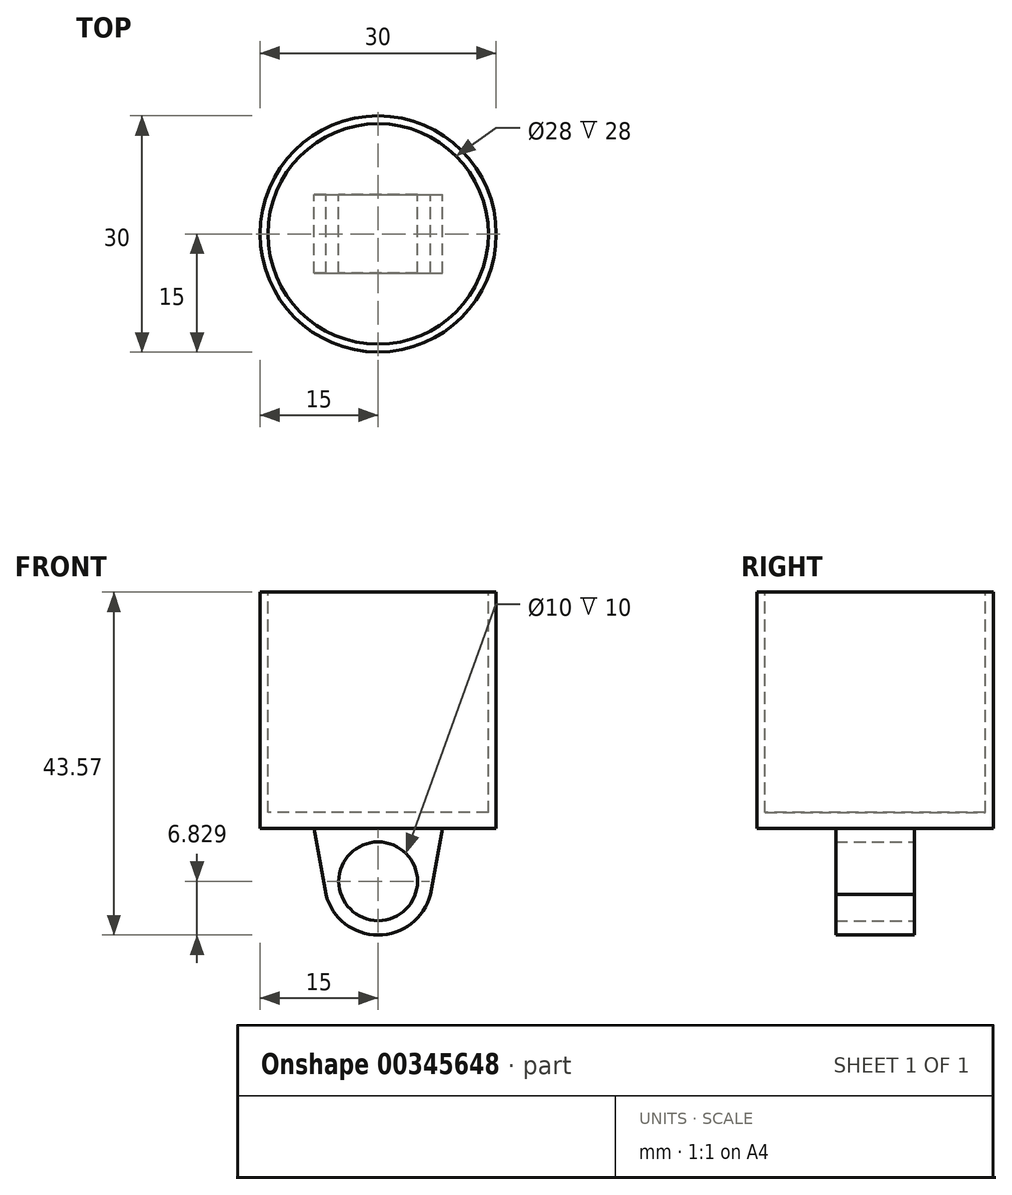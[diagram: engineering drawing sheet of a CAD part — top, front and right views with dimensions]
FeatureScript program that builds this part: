
annotation { "Feature Type Name" : "Feature", "Feature Type Description" : "" }
export const myFeature = defineFeature(function(context is Context, id is Id, definition is map)
    precondition{}
    {
        {
            var Q0;
            Q0=qCreatedBy(makeId("Top.planeOp"),FACE);
            var sketch = newSketch(context, id + "F0", { "sketchPlane" : qUnion([Q0])});
            skCircle(sketch, "E0", {"center": v(0, 0) * mm, "radius": 15 * mm});
            skSolve(sketch);
        }
        {
            var Q0;
            Q0=qSketchRegion(id+"F0",true);
            extrude(context, id + "F1", {"entities" : qUnion([Q0]), "depth" : 30 * mm});
        }
        {
            var Q0;
            Q0=makeQuery(id+"F1.opExtrude","CAP_FACE",FACE,{"disambiguationData":[OSD([sQuery(id+"F0.wireOp",EDGE,"E0")])],"isStart":false});
            var sketch = newSketch(context, id + "F2", { "sketchPlane" : qUnion([Q0])});
            skCircle(sketch, "E1", {"center": v(0, 0) * mm, "radius": 14 * mm});
            skSolve(sketch);
        }
        {
            var Q0;
            Q0=qSketchRegion(id+"F2",true);
            extrude(context, id + "F3", {"entities" : qUnion([Q0]), "operationType" : NewBodyOperationType.REMOVE, "oppositeDirection" : true, "depth" : 28 * mm});
        }
        {
            var Q0;
            Q0=qCreatedBy(makeId("Front.planeOp"),FACE);
            var sketch = newSketch(context, id + "F4", { "sketchPlane" : qUnion([Q0])});
            skArc(sketch, "E2", {"start": v(-6.62, -8.4) * mm, "mid": v(0, -13.57) * mm, "end": v(6.62, -8.4) * mm});
            skLineSegment(sketch, "E3", {"start": v(-6.62, -8.4) * mm, "end": v(-8.16, 0) * mm});
            skLineSegment(sketch, "E4", {"start": v(6.62, -8.4) * mm, "end": v(8.16, 0) * mm});
            skCircle(sketch, "E5", {"center": v(0, -6.74) * mm, "radius": 5 * mm});
            skLineSegment(sketch, "E6", {"start": v(-8.16, 0) * mm, "end": v(8.16, 0) * mm});
            skSolve(sketch);
        }
        {
            var Q0;
            Q0=qSketchRegion(id+"F4",true);
            extrude(context, id + "F5", {"entities" : qUnion([Q0]), "depth" : 10 * mm, "symmetric" : true});
        }
    });
